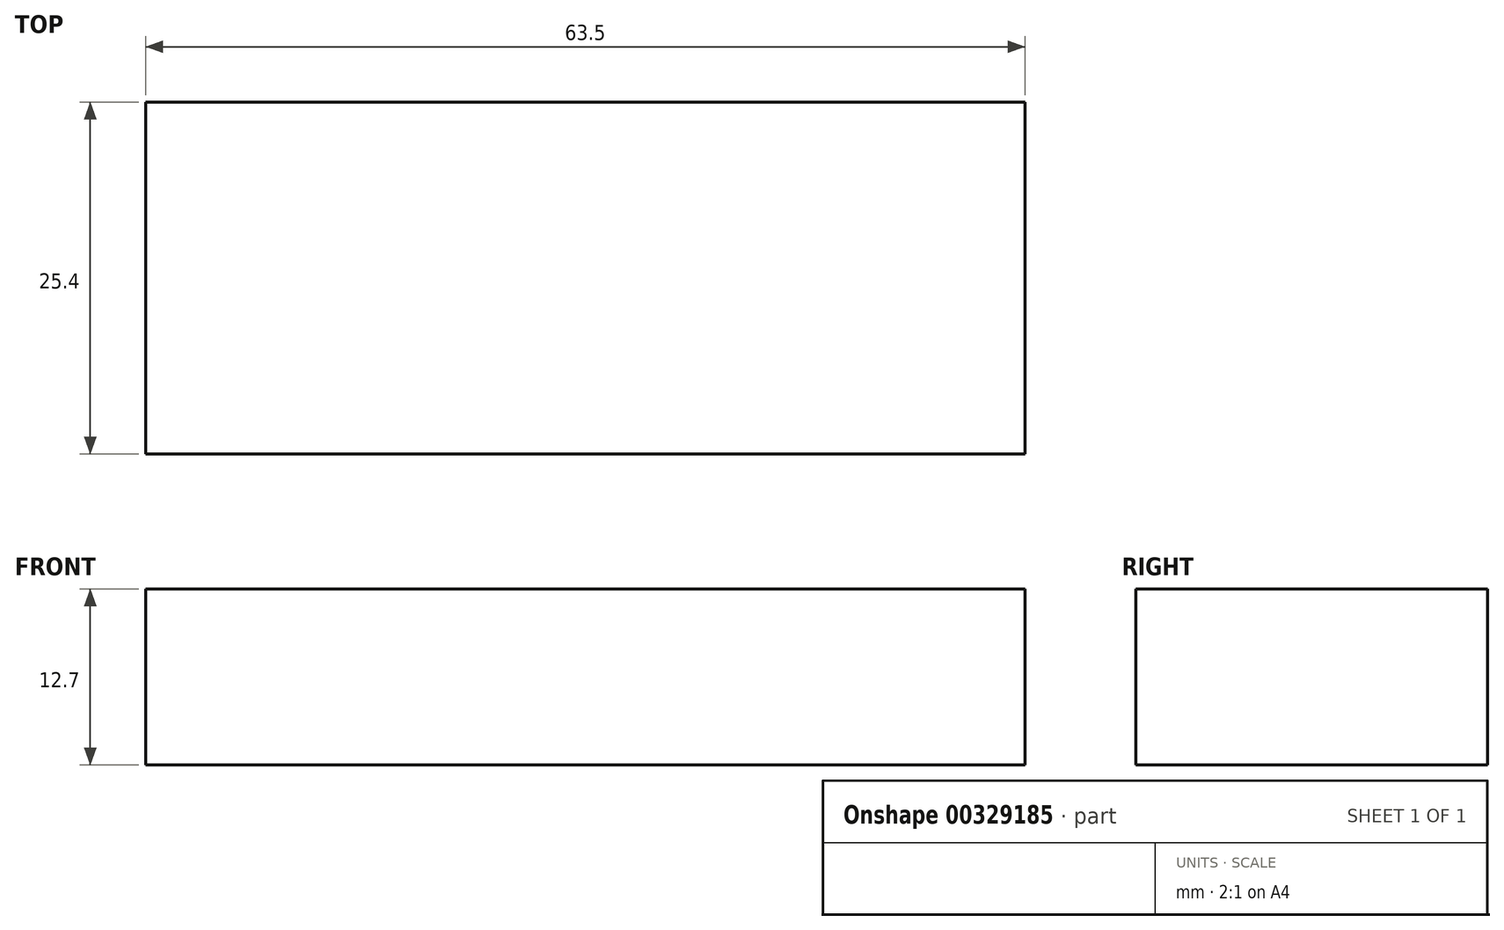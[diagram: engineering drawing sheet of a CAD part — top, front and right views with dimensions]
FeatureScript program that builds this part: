
annotation { "Feature Type Name" : "Feature", "Feature Type Description" : "" }
export const myFeature = defineFeature(function(context is Context, id is Id, definition is map)
    precondition{}
    {
        {
            var Q0;
            Q0=qCreatedBy(makeId("Front.planeOp"),FACE);
            var sketch = newSketch(context, id + "F0", { "sketchPlane" : qUnion([Q0])});
            skLineSegment(sketch, "E0.bottom", {"start": v(0, 0) * mm, "end": v(63.5, 0) * mm});
            skLineSegment(sketch, "E0.top", {"start": v(0, 12.7) * mm, "end": v(63.5, 12.7) * mm});
            skLineSegment(sketch, "E0.left", {"start": v(0, 0) * mm, "end": v(0, 12.7) * mm});
            skLineSegment(sketch, "E0.right", {"start": v(63.5, 0) * mm, "end": v(63.5, 12.7) * mm});
            skLineSegment(sketch, "E1.bottom", {"start": v(15.88, 12.7) * mm, "end": v(47.62, 12.7) * mm});
            skLineSegment(sketch, "E1.top", {"start": v(15.87, 25.4) * mm, "end": v(47.62, 25.4) * mm});
            skLineSegment(sketch, "E1.left", {"start": v(15.87, 12.7) * mm, "end": v(15.87, 25.4) * mm});
            skLineSegment(sketch, "E1.right", {"start": v(47.62, 12.7) * mm, "end": v(47.62, 25.4) * mm});
            skSolve(sketch);
        }
        {
            var Q0;
            Q0=makeQuery(id+"F0.imprint","IMPRINT",FACE,{"disambiguationData":[TD([[makeQuery(id+"F0.imprint","IMPRINT",EDGE,{"derivedFrom":sQuery(id+"F0.wireOp",EDGE,"E0.bottom")}),1.0]])]});
            var Q1;
            Q1=makeQuery(id+"F0.imprint","IMPRINT",FACE,{"disambiguationData":[TD([[makeQuery(id+"F0.imprint","IMPRINT",EDGE,{"derivedFrom":sQuery(id+"F0.wireOp",EDGE,"E1.bottom")}),1.0]])]});
            extrude(context, id + "F1", {"entities" : qUnion([Q0, Q1]), "depth" : 25.4 * mm});
        }
    });
